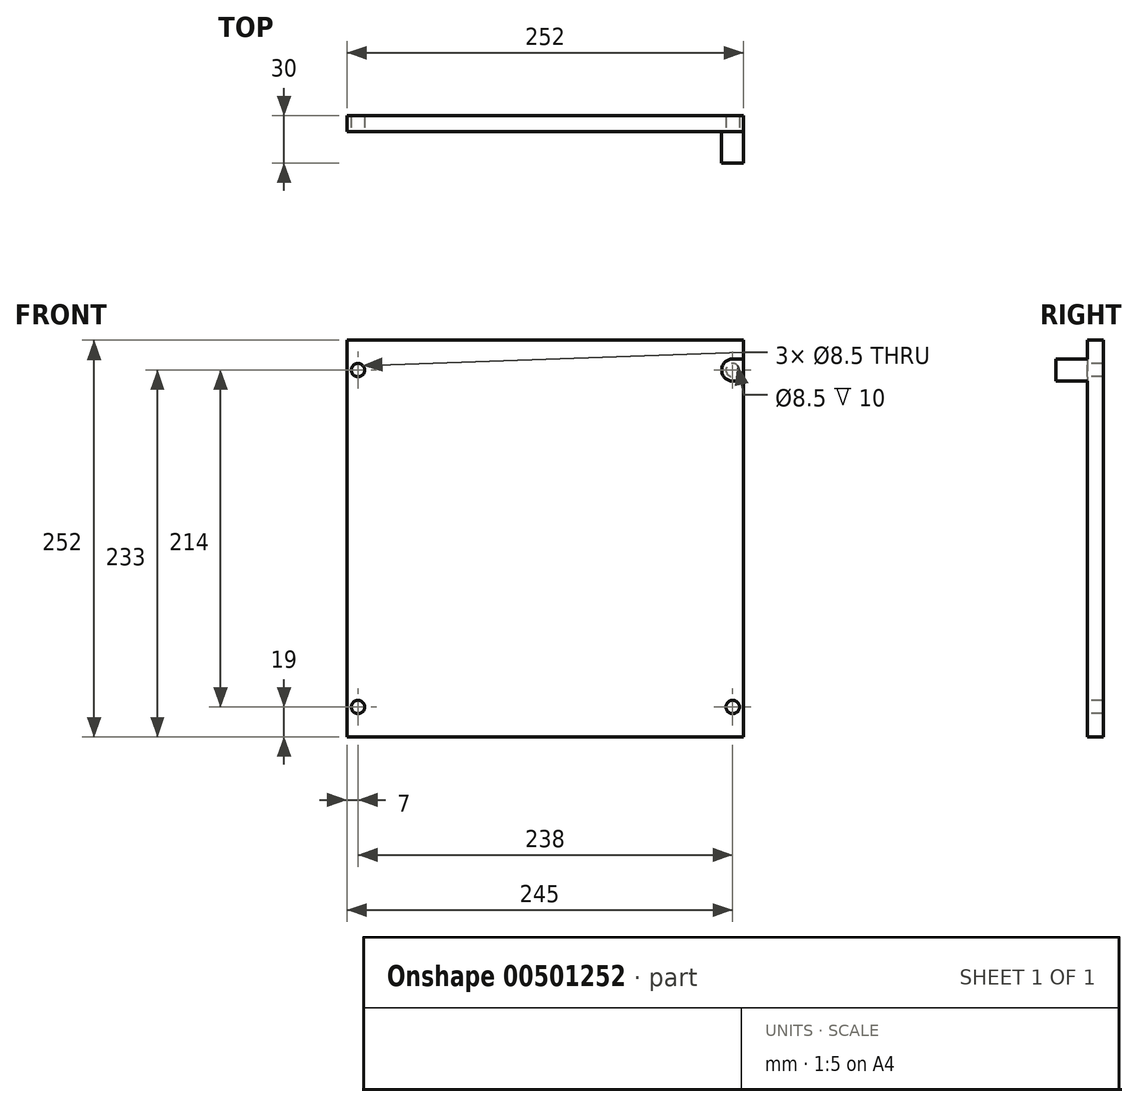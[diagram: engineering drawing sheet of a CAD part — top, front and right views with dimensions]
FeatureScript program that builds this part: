
annotation { "Feature Type Name" : "Feature", "Feature Type Description" : "" }
export const myFeature = defineFeature(function(context is Context, id is Id, definition is map)
    precondition{}
    {
        {
            var Q0;
            Q0=qCreatedBy(makeId("Front.planeOp"),FACE);
            var sketch = newSketch(context, id + "F0", { "sketchPlane" : qUnion([Q0])});
            skLineSegment(sketch, "E0.bottom", {"start": v(0, 0) * mm, "end": v(252, 0) * mm});
            skLineSegment(sketch, "E0.top", {"start": v(0, 252) * mm, "end": v(252, 252) * mm});
            skLineSegment(sketch, "E0.left", {"start": v(0, 0) * mm, "end": v(0, 252) * mm});
            skLineSegment(sketch, "E0.right", {"start": v(252, 0) * mm, "end": v(252, 252) * mm});
            skSolve(sketch);
        }
        {
            var Q0;
            Q0=makeQuery(id+"F0.imprint","IMPRINT",FACE,{"disambiguationData":[TD([[makeQuery(id+"F0.imprint","IMPRINT",EDGE,{"derivedFrom":sQuery(id+"F0.wireOp",EDGE,"E0.bottom")}),1.0]])]});
            extrude(context, id + "F1", {"entities" : qUnion([Q0]), "depth" : 30 * mm});
        }
        {
            var Q0;
            Q0=makeQuery(id+"F1.opExtrude","CAP_FACE",FACE,{"disambiguationData":[OSD([sQuery(id+"F0.wireOp",EDGE,"E0.bottom"),sQuery(id+"F0.wireOp",EDGE,"E0.top"),sQuery(id+"F0.wireOp",EDGE,"E0.left"),sQuery(id+"F0.wireOp",EDGE,"E0.right")])],"isStart":false});
            var sketch = newSketch(context, id + "F2", { "sketchPlane" : qUnion([Q0])});
            skLineSegment(sketch, "E1", {"start": v(0, 126) * mm, "end": v(0, 233) * mm});
            skArc(sketch, "E2", {"start": v(7, 226) * mm, "mid": v(14, 233) * mm, "end": v(7, 240) * mm});
            skLineSegment(sketch, "E3", {"start": v(7, 240) * mm, "end": v(0, 240) * mm});
            skLineSegment(sketch, "E4.MirrorCS", {"start": v(7, 226) * mm, "end": v(0, 226) * mm});
            skLineSegment(sketch, "E5", {"start": v(0, 126) * mm, "end": v(39.65, 126) * mm});
            skLineSegment(sketch, "E6.MirrorCS", {"start": v(7, 26) * mm, "end": v(0, 26) * mm});
            skLineSegment(sketch, "E7.MirrorCS", {"start": v(7, 12) * mm, "end": v(0, 12) * mm});
            skArc(sketch, "E8.MirrorCS", {"start": v(7, 26) * mm, "mid": v(14, 19) * mm, "end": v(7, 12) * mm});
            skLineSegment(sketch, "E9", {"start": v(126, 252) * mm, "end": v(126, 193.94) * mm});
            skPoint(sketch, "E9.endSnap0", {"position": v(126, 252) * mm});
            skArc(sketch, "E10.MirrorCS", {"start": v(245, 226) * mm, "mid": v(238, 233) * mm, "end": v(245, 240) * mm});
            skLineSegment(sketch, "E11.MirrorCS", {"start": v(245, 226) * mm, "end": v(252, 226) * mm});
            skLineSegment(sketch, "E12.MirrorCS", {"start": v(245, 240) * mm, "end": v(252, 240) * mm});
            skLineSegment(sketch, "E13.MirrorCS", {"start": v(245, 12) * mm, "end": v(252, 12) * mm});
            skLineSegment(sketch, "E14.MirrorCS", {"start": v(245, 26) * mm, "end": v(252, 26) * mm});
            skArc(sketch, "E15.MirrorCS", {"start": v(245, 26) * mm, "mid": v(238, 19) * mm, "end": v(245, 12) * mm});
            skSolve(sketch);
        }
        {
            var Q0;
            Q0 = qSketchRegion(id + "F2", true);
            var Q1;
            {var subQ0=sQuery(id+"F2.wireOp",EDGE,"E6.MirrorCS");Q1=makeQuery(id+"F2.imprint","IMPRINT",FACE,{"disambiguationData":[TD([[makeQuery(id+"F2.imprint","IMPRINT",EDGE,{"derivedFrom":subQ0}),1.0]])]});}
            var Q2;
            {var subQ0=sQuery(id+"F2.wireOp",EDGE,"E13.MirrorCS");Q2=makeQuery(id+"F2.imprint","IMPRINT",FACE,{"disambiguationData":[TD([[makeQuery(id+"F2.imprint","IMPRINT",EDGE,{"derivedFrom":subQ0}),1.0]])]});}
            var Q3;
            Q3=makeQuery(id+"F2.imprint","IMPRINT",FACE,{"disambiguationData":[TD([[makeQuery(id+"F2.imprint","IMPRINT",EDGE,{"derivedFrom":sQuery(id+"F2.wireOp",EDGE,"E10.MirrorCS")}),-1.0]])]});
            var Q4;
            Q4=makeQuery(id+"F2.imprint","IMPRINT",FACE,{"disambiguationData":[TD([[makeQuery(id+"F2.imprint","IMPRINT",EDGE,{"derivedFrom":sQuery(id+"F2.wireOp",EDGE,"E2")}),1.0]])]});
            extrude(context, id + "F3", {"entities" : qUnion([Q0, Q1, Q2, Q3, Q4]), "operationType" : NewBodyOperationType.REMOVE, "oppositeDirection" : true, "depth" : 20 * mm});
        }
        {
            var Q0;
            Q0=makeQuery(id+"F3.boolean.opBoolean","COPY",FACE,{"derivedFrom":makeQuery(id+"F3.opExtrude","CAP_FACE",FACE,{"disambiguationData":[OSD([sQuery(id+"F0.wireOp",EDGE,"E0.left"),sQuery(id+"F2.wireOp",EDGE,"E6.MirrorCS"),sQuery(id+"F2.wireOp",EDGE,"E7.MirrorCS"),sQuery(id+"F2.wireOp",EDGE,"E8.MirrorCS")])],"isStart":false})});
            var sketch = newSketch(context, id + "F4", { "sketchPlane" : qUnion([Q0])});
            skCircle(sketch, "E16", {"center": v(7, 19) * mm, "radius": 4.25 * mm});
            skCircle(sketch, "E17.0.1.0", {"center": v(7, 233) * mm, "radius": 4.25 * mm});
            skCircle(sketch, "E17.1.0.0", {"center": v(245, 19) * mm, "radius": 4.25 * mm});
            skCircle(sketch, "E17.1.1.0", {"center": v(245, 233) * mm, "radius": 4.25 * mm});
            skLineSegment(sketch, "E17.direction1", {"start": v(7, 19) * mm, "end": v(245, 19) * mm, "construction": true});
            skLineSegment(sketch, "E17.direction2", {"start": v(7, 19) * mm, "end": v(7, 233) * mm, "construction": true});
            skSolve(sketch);
        }
        {
            var Q0;
            Q0=sQuery(id+"F4.wireOp",VERTEX,"E17.direction2.end");
            var Q1;
            Q1=sQuery(id+"F4.wireOp",VERTEX,"E17.1.1.0.center");
            var Q2;
            Q2=sQuery(id+"F4.wireOp",VERTEX,"E17.1.0.0.center");
            var Q3;
            Q3=sQuery(id+"F4.wireOp",VERTEX,"E16.center");
            var Q4;
            Q4=makeQuery(id+"F1.opExtrude","SWEPT_BODY",BODY,{"disambiguationData":[OSD([sQuery(id+"F0.wireOp",EDGE,"E0.bottom"),sQuery(id+"F0.wireOp",EDGE,"E0.top"),sQuery(id+"F0.wireOp",EDGE,"E0.left"),sQuery(id+"F0.wireOp",EDGE,"E0.right")])]});
            hole(context, id + "F5", {"style" : HoleStyle.SIMPLE, "endStyle" : HoleEndStyle.THROUGH, "holeDiameter" : 8.5 * mm, "isTappedThrough" : true, "tappedDepth" : 12 * mm, "tapClearance" : 3, "locations" : qUnion([Q0, Q1, Q2, Q3]), "scope" : qUnion([Q4])});
        }
    });
